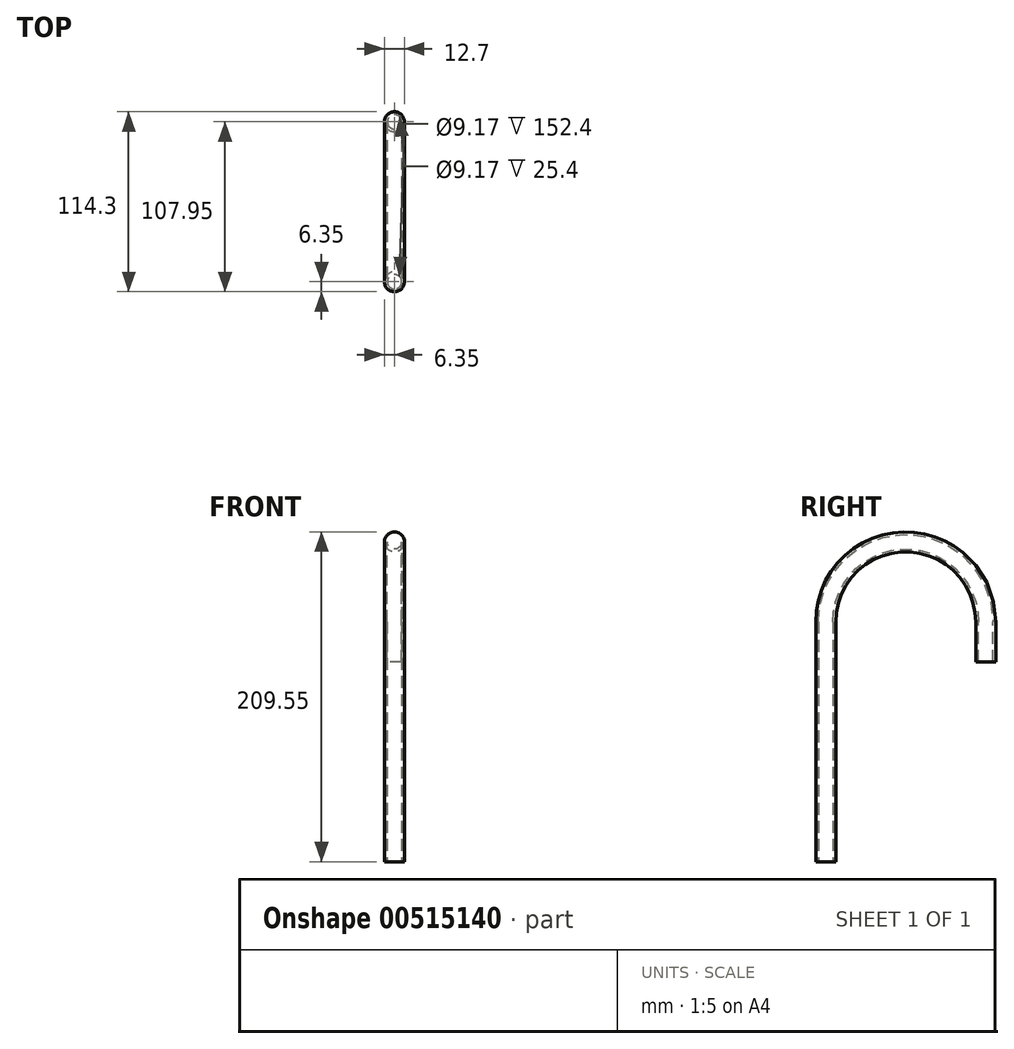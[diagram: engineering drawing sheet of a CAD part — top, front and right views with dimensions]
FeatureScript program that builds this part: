
annotation { "Feature Type Name" : "Feature", "Feature Type Description" : "" }
export const myFeature = defineFeature(function(context is Context, id is Id, definition is map)
    precondition{}
    {
        {
            var Q0;
            Q0=qCreatedBy(makeId("Right.planeOp"),FACE);
            var sketch = newSketch(context, id + "F0", { "sketchPlane" : qUnion([Q0])});
            skLineSegment(sketch, "E0", {"start": v(0, 0) * mm, "end": v(0, 25.4) * mm});
            skArc(sketch, "E1", {"start": v(0, 25.4) * mm, "mid": v(-50.8, 76.2) * mm, "end": v(-101.6, 25.4) * mm});
            skLineSegment(sketch, "E2", {"start": v(-101.6, 25.4) * mm, "end": v(-101.6, -127) * mm});
            skSolve(sketch);
        }
        {
            var Q0;
            Q0=qCreatedBy(makeId("Top.planeOp"),FACE);
            var sketch = newSketch(context, id + "F1", { "sketchPlane" : qUnion([Q0])});
            skCircle(sketch, "E3", {"center": v(0, 0) * mm, "radius": 6.35 * mm});
            skCircle(sketch, "E4", {"center": v(0, 0) * mm, "radius": 4.59 * mm});
            skSolve(sketch);
        }
        {
            var Q0;
            Q0=makeQuery(id+"F1.imprint","IMPRINT",FACE,{"disambiguationData":[TD([[makeQuery(id+"F1.imprint","IMPRINT",EDGE,{"derivedFrom":sQuery(id+"F1.wireOp",EDGE,"E3")}),1.0]])]});
            var Q1;
            Q1=sQuery(id+"F0.wireOp",EDGE,"E0");
            var Q2;
            Q2=sQuery(id+"F0.wireOp",EDGE,"E1");
            var Q3;
            Q3=sQuery(id+"F0.wireOp",EDGE,"E2");
            sweep(context, id + "F2", {"profiles" : qUnion([Q0]), "path" : qUnion([Q1, Q2, Q3])});
        }
    });
